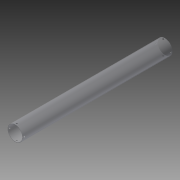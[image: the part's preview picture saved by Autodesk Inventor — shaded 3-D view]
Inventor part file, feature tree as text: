
AUTODESK INVENTOR PART (.ipt)
format: ipt  version: 2014 (Build 180170000, 170)  size: 132,608 bytes
history: native  units: in
note: dims shown in document units (in); Inventor stores cm internally (conversion verified against a paired STEP export)
features: extrude x3, sketch x3, plane x2, projected_geometry x1
ambient origin geometry x8: Origin, YZ Plane, XZ Plane, XY Plane, X Axis, Y Axis, Z Axis, Center Point
bodies: Solid1 (feature_tree)
feature tree (9):
  extrude  "Extrusion1"  Depth=1.875in
  plane  "Work Plane1"
  extrude  "Extrusion2"  Depth=9.8788in
  plane  "Work Plane2"
  extrude  "Extrusion3"  Depth=0.2188in
  sketch  "Sketch1"  dims[d0=2.0in d1=1.875in]
  sketch  "Sketch2"  dims[d2=19.7575in d3=0.0in d4=9.8788in]
  projected_geometry  "Projected Loop1"
  sketch  "Sketch3"  dims[d5=0.19in d6=0.2188in d7=1.0in d8=2.0in d9=0.0in d10=9.8788in d11=0.19in d12=0.2188in d13=1.0in d14=2.0in d15=0.0in]
